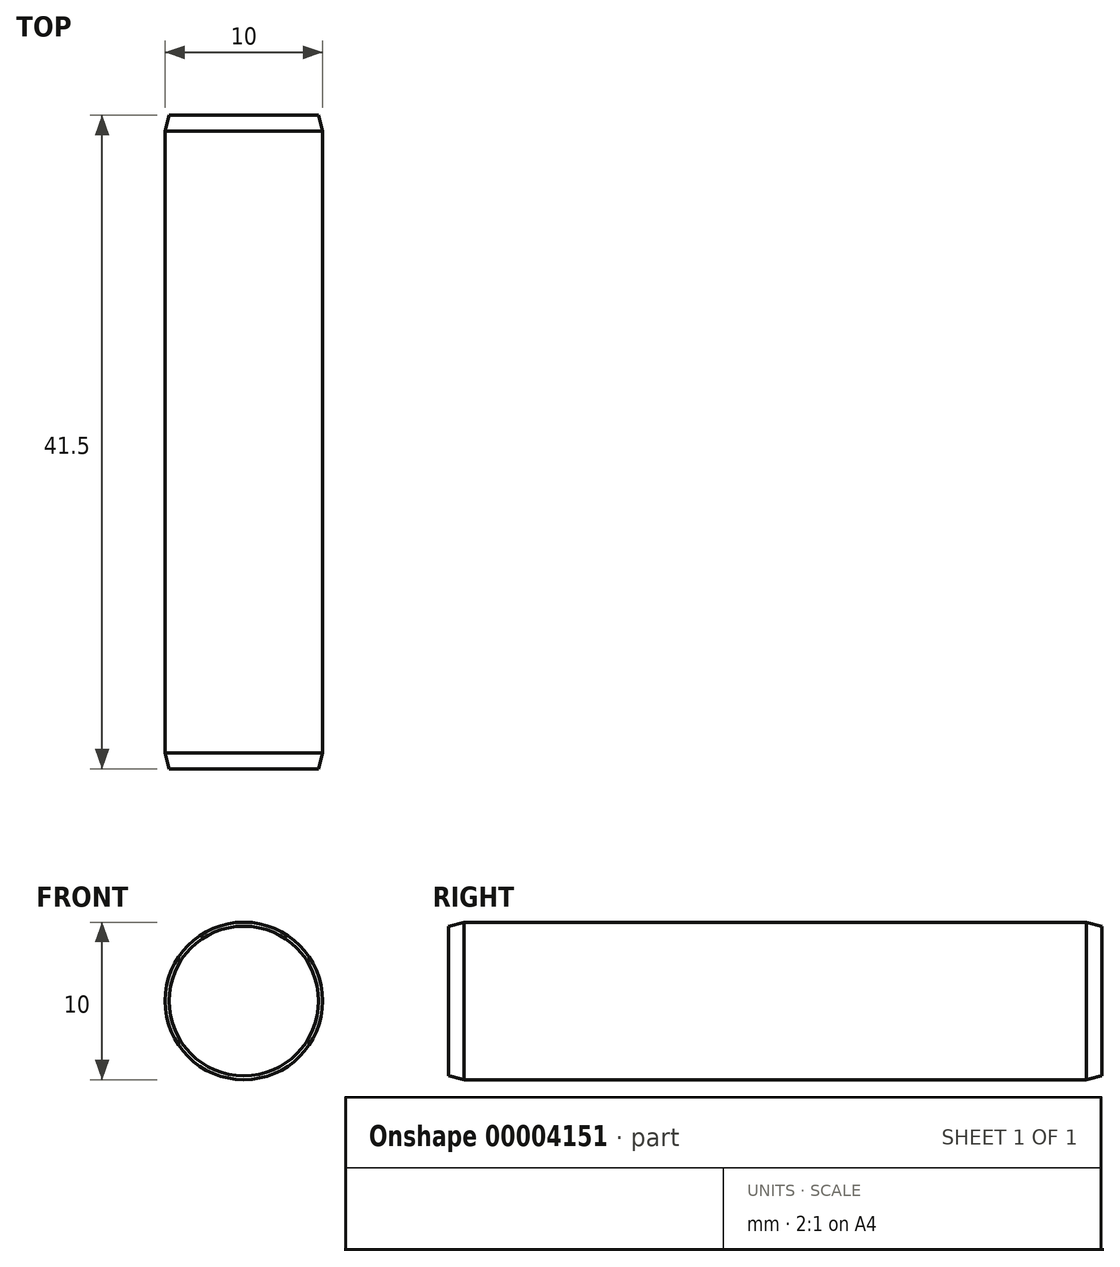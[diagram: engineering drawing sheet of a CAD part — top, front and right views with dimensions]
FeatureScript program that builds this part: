
annotation { "Feature Type Name" : "Feature", "Feature Type Description" : "" }
export const myFeature = defineFeature(function(context is Context, id is Id, definition is map)
    precondition{}
    {
        {
            var Q0;
            Q0=qCreatedBy(makeId("Front.planeOp"),FACE);
            var sketch = newSketch(context, id + "F0", { "sketchPlane" : qUnion([Q0])});
            skCircle(sketch, "E0", {"center": v(0, 0) * mm, "radius": 5 * mm});
            skSolve(sketch);
        }
        {
            var Q0;
            Q0=makeQuery(id+"F0.imprint","IMPRINT",FACE,{"disambiguationData":[TD([[makeQuery(id+"F0.imprint","IMPRINT",EDGE,{"derivedFrom":sQuery(id+"F0.wireOp",EDGE,"E0")}),1.0]])]});
            extrude(context, id + "F1", {"entities" : qUnion([Q0]), "endBound" : BoundingType.SYMMETRIC, "oppositeDirection" : true, "depth" : 41.5 * mm});
        }
        {
            var Q0;
            Q0=makeQuery(id+"F1.opExtrude","CAP_EDGE",EDGE,{"disambiguationData":[OSD([sQuery(id+"F0.wireOp",EDGE,"E0")])],"isStart":true});
            var Q1;
            Q1=makeQuery(id+"F1.opExtrude","CAP_EDGE",EDGE,{"disambiguationData":[OSD([sQuery(id+"F0.wireOp",EDGE,"E0")])],"isStart":false});
            chamfer(context, id + "F2", {"entities" : qUnion([Q0, Q1]), "chamferType" : ChamferType.TWO_OFFSETS, "width1" : .25 * mm, "oppositeDirection" : false, "width2" : 1 * mm, "tangentPropagation" : true});
        }
    });
